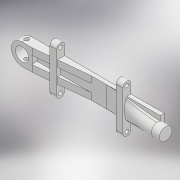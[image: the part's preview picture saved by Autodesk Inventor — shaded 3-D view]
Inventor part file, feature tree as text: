
AUTODESK INVENTOR PART (.ipt)
format: ipt  version: 2018 (Build 220112000, 112)  size: 290,816 bytes
history: native  units: mm
features: sketch x9, extrude x8, plane x3, projected_geometry x2, loft x1, mirror x1, pattern_linear x1
ambient origin geometry x8: Origin, YZ Plane, XZ Plane, XY Plane, X Axis, Y Axis, Z Axis, Center Point
bodies: Solid1 (feature_tree)
feature tree (25):
  sketch  "Sketch1"  dims[d0=10.0mm d2=3.0mm]
  extrude  "Extrusion1"  Depth=3.0mm
  extrude  "Extrusion2"  Depth=16.0mm
  plane  "Work Plane1"
  extrude  "Extrusion3"  Depth=3.0mm TaperAngle=0.0deg
  sketch  "Sketch3"  dims[d5=3.0mm d6=0.0mm d7=4.0mm d8=0.0mm]
  plane  "Work Plane2"
  loft  "Loft1"
  extrude  "Extrusion4"  [1 undecoded]
  extrude  "Extrusion5"  Depth=10.0mm TaperAngle=90.0deg
  mirror  "Mirror1"
  extrude  "Extrusion6"  Depth=5.0mm TaperAngle=0.0deg
  plane  "Work Plane3"
  extrude  "Extrusion14"  Depth=3.2mm
  pattern_linear  "Rectangular Pattern2"  Count1=2  [1 undecoded]
  extrude  "Extrusion13"  Depth=3.0mm
  sketch  "Sketch2"  dims[d3=100.0mm d4=16.0mm]
  projected_geometry  "Projected Loop1"
  sketch  "Sketch4"  dims[d9=6.0mm d10=9.525mm]
  sketch  "Sketch6"  dims[d11=6.0mm d12=0.0mm d13=-40.0mm]
  sketch  "Sketch7"  dims[d14=10.0mm d15=90.0deg d16=10.0mm d17=90.0deg]
  projected_geometry  "Projected Loop2"
  sketch  "Sketch8"  dims[d20=40.0mm d21=5.0mm d22=0.0mm]
  sketch  "Sketch15"  dims[d23=5.0mm d24=0.0mm d25=3.2mm]
  sketch  "Sketch16"  dims[d26=5.0mm d27=0.0mm d75=20.0mm d76=38.5mm d77=3.0mm d78=3.0mm d79=50.0mm d80=22.0mm d81=25.0mm d82=4.0mm d83=22.0mm d84=24.0mm d85=0.0mm d86=3.0mm d87=3.0mm d88=15.0mm d89=30.0mm d90=5.0mm d91=0.0mm d92=20.0mm d94=50.0mm]
note: 2 required parameter values undecoded (feature->parameter linkage not recoverable at this tier; creation-order binding heuristic only, values carry confidence <= 0.55)
